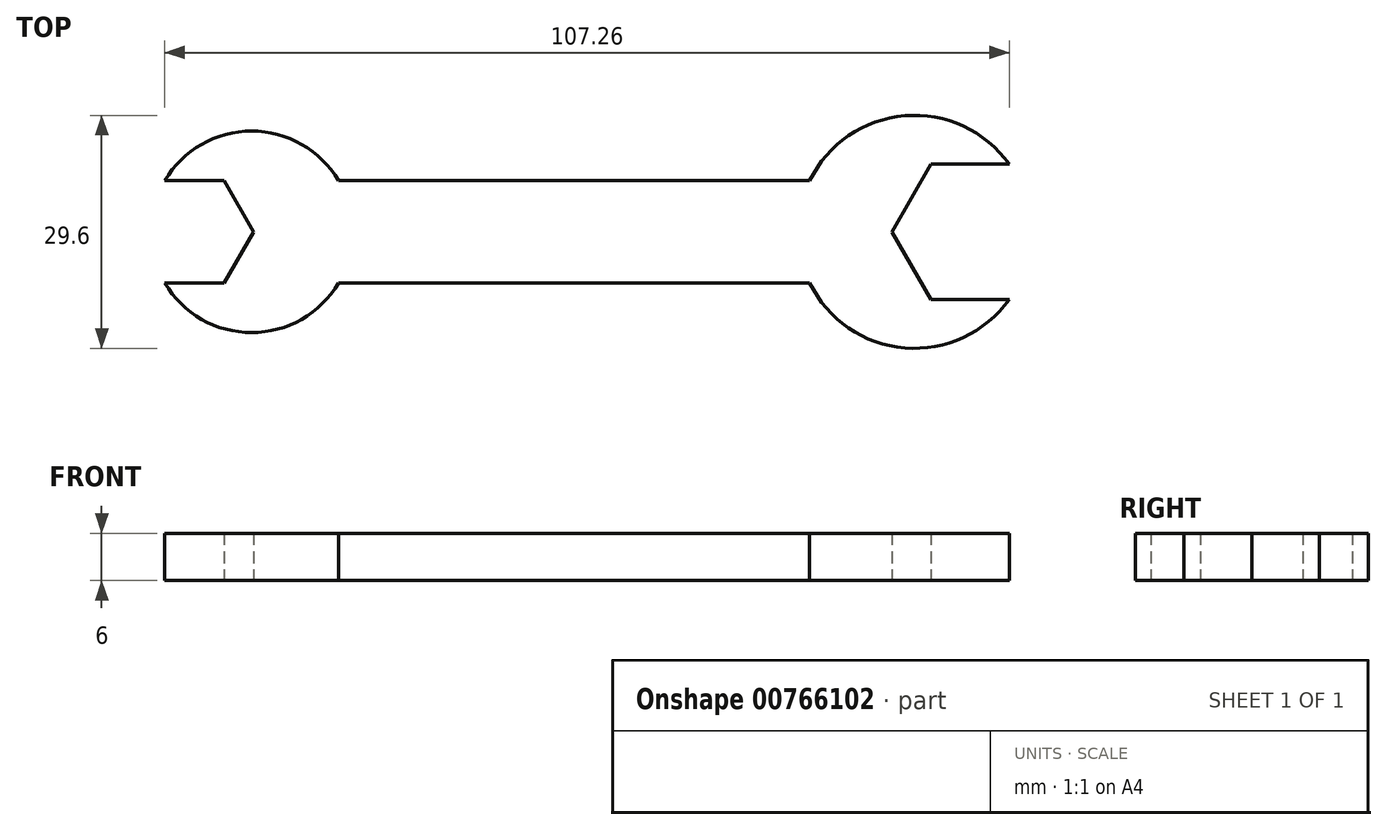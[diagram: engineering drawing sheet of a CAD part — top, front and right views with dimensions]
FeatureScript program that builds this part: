
annotation { "Feature Type Name" : "Feature", "Feature Type Description" : "" }
export const myFeature = defineFeature(function(context is Context, id is Id, definition is map)
    precondition{}
    {
        {
            var Q0;
            Q0=qCreatedBy(makeId("Top.planeOp"),FACE);
            var sketch = newSketch(context, id + "F0", { "sketchPlane" : qUnion([Q0])});
            skLineSegment(sketch, "E0.bottom", {"start": v(-49.65, 6.5) * mm, "end": v(31.45, 6.5) * mm});
            skLineSegment(sketch, "E0.top", {"start": v(-49.65, -6.5) * mm, "end": v(31.45, -6.5) * mm});
            skLineSegment(sketch, "E0.left", {"start": v(-49.65, 6.5) * mm, "end": v(-49.65, -6.5) * mm});
            skLineSegment(sketch, "E0.right", {"start": v(31.45, 6.5) * mm, "end": v(31.45, -6.5) * mm});
            skCircle(sketch, "E1", {"center": v(34.3, 0) * mm, "radius": 14.8 * mm});
            skCircle(sketch, "E2", {"center": v(-49.88, 0) * mm, "radius": 12.8 * mm});
            skCircle(sketch, "E3.cCircle", {"center": v(41.38, 0) * mm, "radius": 9.93 * mm, "construction": true});
            skLineSegment(sketch, "E3.0", {"start": v(46.35, -8.6) * mm, "end": v(36.42, -8.6) * mm});
            skLineSegment(sketch, "E3.1", {"start": v(36.42, -8.6) * mm, "end": v(31.45, 0) * mm});
            skLineSegment(sketch, "E3.2", {"start": v(31.45, 0) * mm, "end": v(36.42, 8.6) * mm});
            skLineSegment(sketch, "E3.3", {"start": v(36.42, 8.6) * mm, "end": v(46.35, 8.6) * mm});
            skLineSegment(sketch, "E3.4", {"start": v(46.35, 8.6) * mm, "end": v(51.32, 0) * mm});
            skLineSegment(sketch, "E3.5", {"start": v(51.32, 0) * mm, "end": v(46.35, -8.6) * mm});
            skCircle(sketch, "E4.cCircle", {"center": v(-57.16, 0) * mm, "radius": 7.5 * mm, "construction": true});
            skLineSegment(sketch, "E4.0", {"start": v(-60.9, 6.5) * mm, "end": v(-53.4, 6.5) * mm});
            skLineSegment(sketch, "E4.1", {"start": v(-53.4, 6.5) * mm, "end": v(-49.65, 0) * mm});
            skLineSegment(sketch, "E4.2", {"start": v(-49.65, 0) * mm, "end": v(-53.4, -6.5) * mm});
            skLineSegment(sketch, "E4.3", {"start": v(-53.4, -6.5) * mm, "end": v(-60.9, -6.5) * mm});
            skLineSegment(sketch, "E4.4", {"start": v(-60.9, -6.5) * mm, "end": v(-64.66, 0) * mm});
            skLineSegment(sketch, "E4.5", {"start": v(-64.66, 0) * mm, "end": v(-60.9, 6.5) * mm});
            skSolve(sketch);
        }
        {
            var Q0;
            {var subQ0=sQuery(id+"F0.wireOp",EDGE,"E4.0");Q0=makeQuery(id+"F0.imprint","IMPRINT",FACE,{"disambiguationData":[TD([[makeQuery(id+"F0.imprint","IMPRINT",EDGE,{"derivedFrom":subQ0}),1.0]])]});}
            var Q1;
            {var subQ0=sQuery(id+"F0.wireOp",EDGE,"E0.left");var subQ4=sQuery(id+"F0.wireOp",EDGE,"E0.bottom");var subQ5=makeQuery(id+"F0.imprint","INTERSECT",VERTEX,{"derivedFrom":[subQ4,subQ0]});Q1=makeQuery(id+"F0.imprint","IMPRINT",FACE,{"disambiguationData":[TD([[makeQuery(id+"F0.imprint","IMPRINT",EDGE,{"disambiguationData":[TD([[subQ5,-1.0]])],"derivedFrom":subQ4}),-1.0]])]});}
            var Q2;
            {var subQ4=sQuery(id+"F0.wireOp",EDGE,"E4.2");Q2=makeQuery(id+"F0.imprint","IMPRINT",FACE,{"disambiguationData":[TD([[makeQuery(id+"F0.imprint","IMPRINT",EDGE,{"derivedFrom":subQ4}),1.0]])]});}
            var Q3;
            {var subQ0=sQuery(id+"F0.wireOp",EDGE,"E2");var subQ1=sQuery(id+"F0.wireOp",EDGE,"E0.bottom");var subQ2=makeQuery(id+"F0.imprint","INTERSECT",VERTEX,{"derivedFrom":[subQ1,subQ0]});Q3=makeQuery(id+"F0.imprint","IMPRINT",FACE,{"disambiguationData":[TD([[makeQuery(id+"F0.imprint","IMPRINT",EDGE,{"disambiguationData":[TD([[subQ2,-1.0]])],"derivedFrom":subQ1}),-1.0]])]});}
            var Q4;
            {var subQ0=sQuery(id+"F0.wireOp",EDGE,"E3.2");Q4=makeQuery(id+"F0.imprint","IMPRINT",FACE,{"disambiguationData":[TD([[makeQuery(id+"F0.imprint","IMPRINT",EDGE,{"derivedFrom":subQ0}),1.0]])]});}
            var Q5;
            {var subQ0=sQuery(id+"F0.wireOp",EDGE,"E0.right");var subQ4=sQuery(id+"F0.wireOp",EDGE,"E0.bottom");var subQ5=makeQuery(id+"F0.imprint","INTERSECT",VERTEX,{"derivedFrom":[subQ4,subQ0]});Q5=makeQuery(id+"F0.imprint","IMPRINT",FACE,{"disambiguationData":[TD([[makeQuery(id+"F0.imprint","IMPRINT",EDGE,{"disambiguationData":[TD([[subQ5,1.0]])],"derivedFrom":subQ4}),-1.0]])]});}
            var Q6;
            {var subQ0=sQuery(id+"F0.wireOp",EDGE,"E3.0");Q6=makeQuery(id+"F0.imprint","IMPRINT",FACE,{"disambiguationData":[TD([[makeQuery(id+"F0.imprint","IMPRINT",EDGE,{"derivedFrom":subQ0}),1.0]])]});}
            extrude(context, id + "F1", {"entities" : qUnion([Q0, Q1, Q2, Q3, Q4, Q5, Q6]), "depth" : 6 * mm, "offsetDistance" : 25 * mm});
        }
    });
